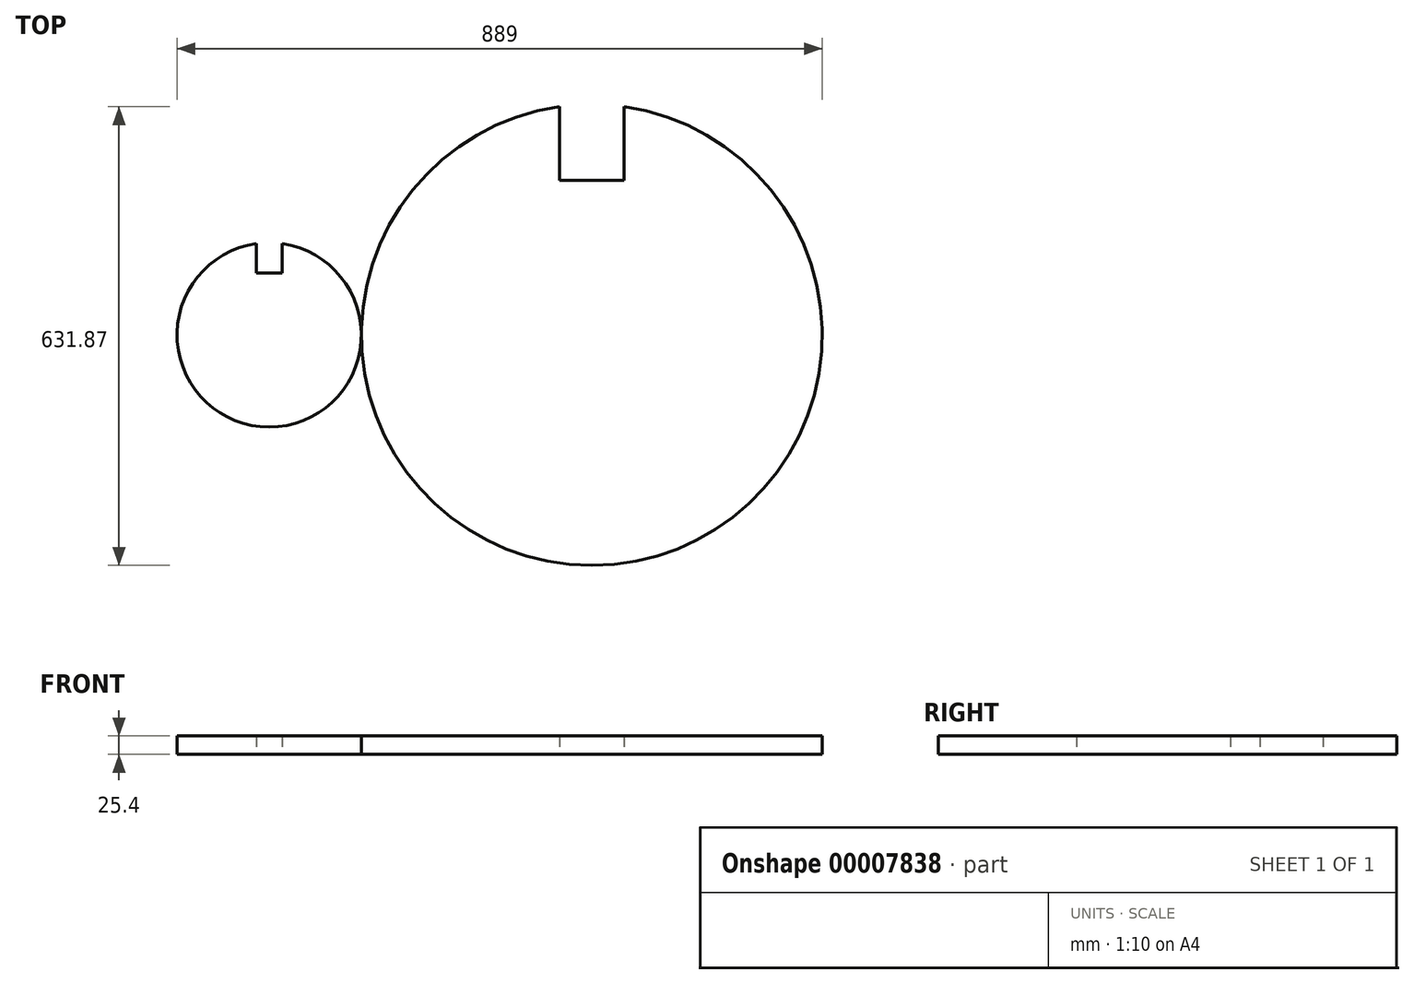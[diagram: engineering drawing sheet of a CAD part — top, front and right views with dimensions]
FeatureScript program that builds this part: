
annotation { "Feature Type Name" : "Feature", "Feature Type Description" : "" }
export const myFeature = defineFeature(function(context is Context, id is Id, definition is map)
    precondition{}
    {
        {
            var Q0;
            Q0=qCreatedBy(makeId("Top.planeOp"),FACE);
            var sketch = newSketch(context, id + "F0", { "sketchPlane" : qUnion([Q0])});
            skCircle(sketch, "E0", {"center": v(0, 0) * mm, "radius": 317.5 * mm});
            skCircle(sketch, "E1", {"center": v(-444.5, 0) * mm, "radius": 127 * mm});
            skLineSegment(sketch, "E2", {"start": v(-444.5, 0) * mm, "end": v(-444.5, 127) * mm, "construction": true});
            skLineSegment(sketch, "E3", {"start": v(0, 0) * mm, "end": v(0, 317.5) * mm, "construction": true});
            skLineSegment(sketch, "E4", {"start": v(-44.45, 314.37) * mm, "end": v(-44.45, 212.77) * mm});
            skLineSegment(sketch, "E5", {"start": v(-44.45, 212.77) * mm, "end": v(44.45, 212.77) * mm});
            skLineSegment(sketch, "E6", {"start": v(44.45, 212.77) * mm, "end": v(44.45, 314.37) * mm});
            skLineSegment(sketch, "E7", {"start": v(-462.28, 125.75) * mm, "end": v(-462.28, 85.1) * mm});
            skLineSegment(sketch, "E8", {"start": v(-462.28, 85.1) * mm, "end": v(-426.72, 85.1) * mm});
            skLineSegment(sketch, "E9", {"start": v(-426.72, 85.1) * mm, "end": v(-426.72, 125.75) * mm});
            skSolve(sketch);
        }
        {
            var Q0;
            {var subQ1=sQuery(id+"F0.wireOp",EDGE,"E4");Q0=makeQuery(id+"F0.imprint","IMPRINT",FACE,{"disambiguationData":[TD([[makeQuery(id+"F0.imprint","IMPRINT",EDGE,{"derivedFrom":subQ1}),-1.0]])]});}
            var Q1;
            {var subQ1=sQuery(id+"F0.wireOp",EDGE,"E7");Q1=makeQuery(id+"F0.imprint","IMPRINT",FACE,{"disambiguationData":[TD([[makeQuery(id+"F0.imprint","IMPRINT",EDGE,{"derivedFrom":subQ1}),-1.0]])]});}
            extrude(context, id + "F1", {"entities" : qUnion([Q0, Q1]), "depth" : 25.4 * mm});
        }
    });
